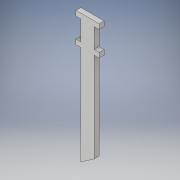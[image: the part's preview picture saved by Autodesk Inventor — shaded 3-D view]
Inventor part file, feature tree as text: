
AUTODESK INVENTOR PART (.ipt)
format: ipt  version: 2017 (Build 210142000, 142)  size: 121,856 bytes
history: native  units: in
note: dims shown in document units (in); Inventor stores cm internally (conversion verified against a paired STEP export)
features: extrude x2, sketch x2
ambient origin geometry x8: Origin, YZ Plane, XZ Plane, XY Plane, X Axis, Y Axis, Z Axis, Center Point
bodies: Body1 (feature_tree)
feature tree (4):
  extrude  "Extrusion1"  Depth=0.1181in TaperAngle=0.0deg
  extrude  "Extrusion2"  Depth=0.7087in
  sketch  "Sketch2"  dims[d3=0.8589in d7=0.1181in d8=0.0in]
  sketch  "Sketch3"  dims[d9=0.315in d10=0.7087in d11=0.1181in d12=2.2605in d13=0.1181in d14=0.7087in d15=0.1181in d16=0.4724in d17=0.1181in d18=0.3937in d19=0.0in]
